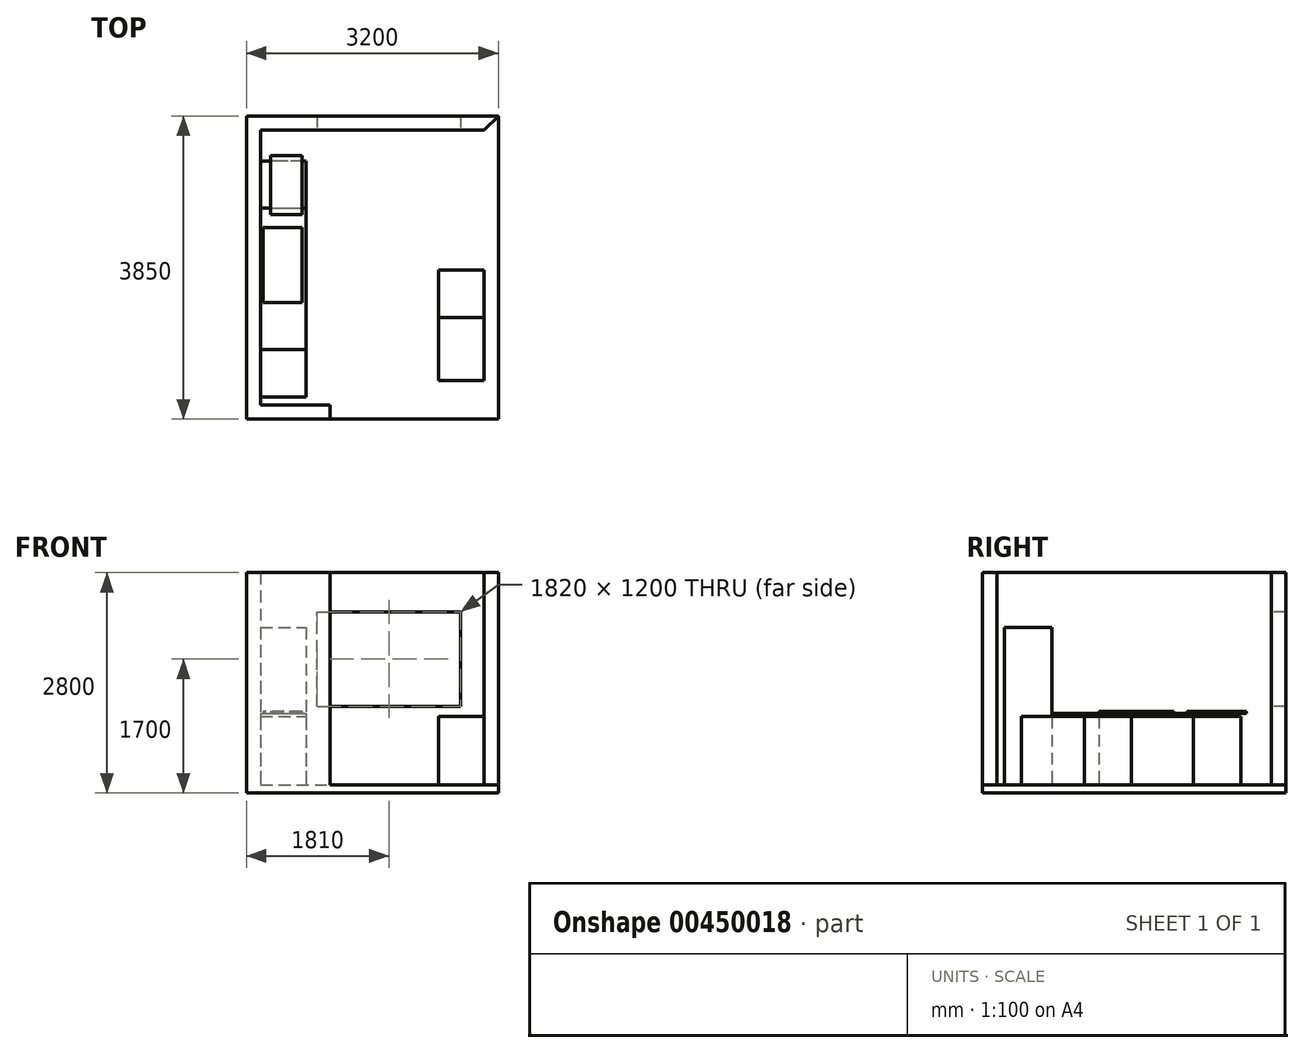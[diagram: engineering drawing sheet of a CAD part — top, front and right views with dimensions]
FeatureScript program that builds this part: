
annotation { "Feature Type Name" : "Feature", "Feature Type Description" : "" }
export const myFeature = defineFeature(function(context is Context, id is Id, definition is map)
    precondition{}
    {
        {
            var Q0;
            Q0=qCreatedBy(makeId("Top.planeOp"),FACE);
            var sketch = newSketch(context, id + "F0", { "sketchPlane" : qUnion([Q0])});
            skLineSegment(sketch, "E0.bottom", {"start": v(0, 0) * mm, "end": v(2840, 0) * mm});
            skLineSegment(sketch, "E0.top", {"start": v(0, 3490) * mm, "end": v(2840, 3490) * mm});
            skLineSegment(sketch, "E0.left", {"start": v(0, 0) * mm, "end": v(0, 3490) * mm});
            skLineSegment(sketch, "E0.right", {"start": v(2840, 0) * mm, "end": v(2840, 3490) * mm});
            skLineSegment(sketch, "E1.0", {"start": v(-180, -180) * mm, "end": v(-180, 3670) * mm});
            skLineSegment(sketch, "E1.1", {"start": v(-180, -180) * mm, "end": v(3020, -180) * mm});
            skLineSegment(sketch, "E1.2", {"start": v(3020, -180) * mm, "end": v(3020, 3670) * mm});
            skLineSegment(sketch, "E1.3", {"start": v(-180, 3670) * mm, "end": v(3020, 3670) * mm});
            skLineSegment(sketch, "E2", {"start": v(2840, 3490) * mm, "end": v(3020, 3670) * mm});
            skLineSegment(sketch, "E3", {"start": v(880, 0) * mm, "end": v(880, -180) * mm});
            skSolve(sketch);
        }
        {
            var Q0;
            Q0=makeQuery(id+"F0.imprint","IMPRINT",FACE,{"disambiguationData":[TD([[makeQuery(id+"F0.imprint","IMPRINT",EDGE,{"derivedFrom":sQuery(id+"F0.wireOp",EDGE,"E0.top")}),1.0]])]});
            var Q1;
            Q1=makeQuery(id+"F0.imprint","IMPRINT",FACE,{"disambiguationData":[TD([[makeQuery(id+"F0.imprint","IMPRINT",EDGE,{"derivedFrom":sQuery(id+"F0.wireOp",EDGE,"E0.top")}),-1.0]])]});
            var Q2;
            {var subQ3=sQuery(id+"F0.wireOp",EDGE,"E0.right");Q2=makeQuery(id+"F0.imprint","IMPRINT",FACE,{"disambiguationData":[TD([[makeQuery(id+"F0.imprint","IMPRINT",EDGE,{"derivedFrom":subQ3}),-1.0]])]});}
            extrude(context, id + "F1", {"entities" : qUnion([Q0, Q1, Q2]), "oppositeDirection" : true, "depth" : 100 * mm});
        }
        {
            var Q0;
            Q0=makeQuery(id+"F0.imprint","IMPRINT",FACE,{"disambiguationData":[TD([[makeQuery(id+"F0.imprint","IMPRINT",EDGE,{"derivedFrom":sQuery(id+"F0.wireOp",EDGE,"E0.top")}),1.0]])]});
            extrude(context, id + "F2", {"entities" : qUnion([Q0]), "operationType" : NewBodyOperationType.ADD, "depth" : 2700 * mm});
        }
        {
            var Q0;
            Q0=makeQuery(id+"F0.imprint","IMPRINT",FACE,{"disambiguationData":[TD([[makeQuery(id+"F0.imprint","IMPRINT",EDGE,{"derivedFrom":sQuery(id+"F0.wireOp",EDGE,"E0.top")}),-1.0]])]});
            var sketch = newSketch(context, id + "F3", { "sketchPlane" : qUnion([Q0])});
            skLineSegment(sketch, "E4.0.0", {"start": v(2840, 3490) * mm, "end": v(0, 3490) * mm});
            skLineSegment(sketch, "E4.0.1", {"start": v(0, 3490) * mm, "end": v(0, 0) * mm});
            skLineSegment(sketch, "E4.0.2", {"start": v(0, 0) * mm, "end": v(880, 0) * mm});
            skLineSegment(sketch, "E4.0.3", {"start": v(880, 0) * mm, "end": v(2840, 0) * mm});
            skLineSegment(sketch, "E4.0.4", {"start": v(2840, 0) * mm, "end": v(2840, 3490) * mm});
            skLineSegment(sketch, "E5.bottom", {"start": v(0, 100) * mm, "end": v(580, 100) * mm});
            skLineSegment(sketch, "E5.top", {"start": v(0, 700) * mm, "end": v(580, 700) * mm});
            skLineSegment(sketch, "E5.left", {"start": v(0, 100) * mm, "end": v(0, 700) * mm});
            skLineSegment(sketch, "E5.right", {"start": v(580, 100) * mm, "end": v(580, 700) * mm});
            skLineSegment(sketch, "E6", {"start": v(580, 700) * mm, "end": v(580, 1300) * mm});
            skLineSegment(sketch, "E7", {"start": v(0, 1300) * mm, "end": v(580, 1300) * mm});
            skLineSegment(sketch, "E8", {"start": v(580, 1300) * mm, "end": v(580, 2500) * mm});
            skLineSegment(sketch, "E9", {"start": v(0, 2500) * mm, "end": v(580, 2500) * mm});
            skLineSegment(sketch, "E10", {"start": v(580, 2500) * mm, "end": v(580, 3100) * mm});
            skLineSegment(sketch, "E11", {"start": v(580, 3100) * mm, "end": v(0, 3100) * mm});
            skLineSegment(sketch, "E12", {"start": v(0, 700) * mm, "end": v(0, 100) * mm});
            skLineSegment(sketch, "E13", {"start": v(0, 700) * mm, "end": v(0, 1300) * mm});
            skLineSegment(sketch, "E14", {"start": v(580, 1300) * mm, "end": v(580, 700) * mm});
            skLineSegment(sketch, "E15", {"start": v(0, 1300) * mm, "end": v(0, 2500) * mm});
            skLineSegment(sketch, "E16", {"start": v(580, 2500) * mm, "end": v(580, 1300) * mm});
            skLineSegment(sketch, "E17", {"start": v(0, 2500) * mm, "end": v(0, 3100) * mm});
            skLineSegment(sketch, "E18", {"start": v(0, 3100) * mm, "end": v(580, 3100) * mm});
            skLineSegment(sketch, "E19", {"start": v(580, 3100) * mm, "end": v(580, 2500) * mm});
            skSolve(sketch);
        }
        {
            var Q0;
            Q0=makeQuery(id+"F3.imprint","IMPRINT",FACE,{"disambiguationData":[TD([[makeQuery(id+"F3.imprint","IMPRINT",EDGE,{"derivedFrom":sQuery(id+"F3.wireOp",EDGE,"E5.bottom")}),1.0]])]});
            extrude(context, id + "F4", {"entities" : qUnion([Q0]), "depth" : 2000 * mm});
        }
        {
            var Q0;
            Q0=makeQuery(id+"F3.imprint","IMPRINT",FACE,{"disambiguationData":[TD([[makeQuery(id+"F3.imprint","IMPRINT",EDGE,{"derivedFrom":sQuery(id+"F3.wireOp",EDGE,"E5.top")}),1.0]])]});
            extrude(context, id + "F5", {"entities" : qUnion([Q0]), "depth" : 870 * mm});
        }
        {
            var Q0;
            Q0=makeQuery(id+"F3.imprint","IMPRINT",FACE,{"disambiguationData":[TD([[makeQuery(id+"F3.imprint","IMPRINT",EDGE,{"derivedFrom":sQuery(id+"F3.wireOp",EDGE,"E7")}),1.0]])]});
            extrude(context, id + "F6", {"entities" : qUnion([Q0]), "depth" : 870 * mm});
        }
        {
            var Q0;
            Q0=makeQuery(id+"F3.imprint","IMPRINT",FACE,{"disambiguationData":[TD([[makeQuery(id+"F3.imprint","IMPRINT",EDGE,{"derivedFrom":sQuery(id+"F3.wireOp",EDGE,"E9")}),1.0]])]});
            extrude(context, id + "F7", {"entities" : qUnion([Q0]), "depth" : 870 * mm});
        }
        {
            var Q0;
            Q0=makeQuery(id+"F6.opExtrude","CAP_FACE",FACE,{"disambiguationData":[OSD([sQuery(id+"F3.wireOp",EDGE,"E7"),sQuery(id+"F3.wireOp",EDGE,"E15"),sQuery(id+"F3.wireOp",EDGE,"E9"),sQuery(id+"F3.wireOp",EDGE,"E16")])],"isStart":false});
            var sketch = newSketch(context, id + "F8", { "sketchPlane" : qUnion([Q0])});
            skLineSegment(sketch, "E20.0", {"start": v(0, 700) * mm, "end": v(580, 700) * mm});
            skLineSegment(sketch, "E21.0", {"start": v(0, 700) * mm, "end": v(0, 1300) * mm});
            skPoint(sketch, "E22.0", {"position": v(0, 3490) * mm});
            skLineSegment(sketch, "E23.0", {"start": v(580, 1300) * mm, "end": v(580, 700) * mm});
            skLineSegment(sketch, "E24.0", {"start": v(2840, 3490) * mm, "end": v(0, 3490) * mm});
            skLineSegment(sketch, "E25", {"start": v(580, 700) * mm, "end": v(580, 3490) * mm});
            skLineSegment(sketch, "E26", {"start": v(580, 3490) * mm, "end": v(0, 3490) * mm});
            skLineSegment(sketch, "E27", {"start": v(0, 2500) * mm, "end": v(0, 3490) * mm});
            skSolve(sketch);
        }
        {
            var Q0;
            {var subQ2=sQuery(id+"F8.wireOp",EDGE,"E26");Q0=makeQuery(id+"F8.imprint","IMPRINT",FACE,{"disambiguationData":[TD([[makeQuery(id+"F8.imprint","IMPRINT",EDGE,{"derivedFrom":subQ2}),1.0]])]});}
            var Q1;
            {var subQ1=makeQuery(id+"F6.opExtrude","CAP_EDGE",EDGE,{"disambiguationData":[OSD([sQuery(id+"F3.wireOp",EDGE,"E7")])],"isStart":false});Q1=makeQuery(id+"F8.imprint","IMPRINT",FACE,{"disambiguationData":[TD([[makeQuery(id+"F8.imprint","IMPRINT",EDGE,{"derivedFrom":subQ1}),1.0]])]});}
            var Q2;
            Q2=makeQuery(id+"F8.imprint","IMPRINT",FACE,{"disambiguationData":[TD([[makeQuery(id+"F8.imprint","IMPRINT",EDGE,{"derivedFrom":sQuery(id+"F8.wireOp",EDGE,"E21.0")}),-1.0]])]});
            extrude(context, id + "F9", {"entities" : qUnion([Q0, Q1, Q2]), "depth" : 40 * mm});
        }
        {
            var Q0;
            Q0=makeQuery(id+"F9.opExtrude","CAP_FACE",FACE,{"disambiguationData":[OSD([sQuery(id+"F3.wireOp",EDGE,"E15"),sQuery(id+"F8.wireOp",EDGE,"E21.0"),sQuery(id+"F8.wireOp",EDGE,"E20.0"),sQuery(id+"F8.wireOp",EDGE,"E25"),sQuery(id+"F8.wireOp",EDGE,"E26"),sQuery(id+"F8.wireOp",EDGE,"E27")])],"isStart":false});
            var sketch = newSketch(context, id + "F10", { "sketchPlane" : qUnion([Q0])});
            skLineSegment(sketch, "E28.0", {"start": v(580, 3100) * mm, "end": v(0, 3100) * mm});
            skLineSegment(sketch, "E29.0", {"start": v(0, 2500) * mm, "end": v(580, 2500) * mm});
            skPoint(sketch, "E30.0", {"position": v(580, 2800) * mm});
            skLineSegment(sketch, "E31.bottom", {"start": v(130, 3167.5) * mm, "end": v(530, 3167.5) * mm});
            skLineSegment(sketch, "E31.top", {"start": v(130, 2417.5) * mm, "end": v(530, 2417.5) * mm});
            skLineSegment(sketch, "E31.left", {"start": v(130, 3167.5) * mm, "end": v(130, 2417.5) * mm});
            skLineSegment(sketch, "E31.right", {"start": v(530, 3167.5) * mm, "end": v(530, 2417.5) * mm});
            skSolve(sketch);
        }
        {
            var Q0;
            {var subQ5=sQuery(id+"F10.wireOp",EDGE,"E31.bottom");Q0=makeQuery(id+"F10.imprint","IMPRINT",FACE,{"disambiguationData":[TD([[makeQuery(id+"F10.imprint","IMPRINT",EDGE,{"derivedFrom":subQ5}),-1.0]])]});}
            var Q1;
            {var subQ0=sQuery(id+"F10.wireOp",EDGE,"E31.right");var subQ1=sQuery(id+"F10.wireOp",EDGE,"E28.0");var subQ2=makeQuery(id+"F10.imprint","INTERSECT",VERTEX,{"derivedFrom":[subQ1,subQ0]});Q1=makeQuery(id+"F10.imprint","IMPRINT",FACE,{"disambiguationData":[TD([[makeQuery(id+"F10.imprint","IMPRINT",EDGE,{"disambiguationData":[TD([[subQ2,-1.0]])],"derivedFrom":subQ1}),1.0]])]});}
            var Q2;
            {var subQ5=sQuery(id+"F10.wireOp",EDGE,"E31.top");Q2=makeQuery(id+"F10.imprint","IMPRINT",FACE,{"disambiguationData":[TD([[makeQuery(id+"F10.imprint","IMPRINT",EDGE,{"derivedFrom":subQ5}),1.0]])]});}
            extrude(context, id + "F11", {"entities" : qUnion([Q0, Q1, Q2]), "depth" : 25 * mm});
        }
        {
            var Q0;
            Q0=makeQuery(id+"F9.opExtrude","CAP_FACE",FACE,{"disambiguationData":[OSD([sQuery(id+"F3.wireOp",EDGE,"E15"),sQuery(id+"F8.wireOp",EDGE,"E21.0"),sQuery(id+"F8.wireOp",EDGE,"E20.0"),sQuery(id+"F8.wireOp",EDGE,"E25"),sQuery(id+"F8.wireOp",EDGE,"E26"),sQuery(id+"F8.wireOp",EDGE,"E27")])],"isStart":false});
            var sketch = newSketch(context, id + "F12", { "sketchPlane" : qUnion([Q0])});
            skLineSegment(sketch, "E32.0", {"start": v(0, 1300) * mm, "end": v(580, 1300) * mm, "construction": true});
            skLineSegment(sketch, "E33.0", {"start": v(580, 1300) * mm, "end": v(580, 2500) * mm, "construction": true});
            skLineSegment(sketch, "E34.0", {"start": v(0, 2500) * mm, "end": v(580, 2500) * mm, "construction": true});
            skLineSegment(sketch, "E35.bottom", {"start": v(530, 1300) * mm, "end": v(30, 1300) * mm, "construction": true});
            skLineSegment(sketch, "E35.top", {"start": v(530, 2250) * mm, "end": v(30, 2250) * mm, "construction": true});
            skLineSegment(sketch, "E35.left", {"start": v(530, 1300) * mm, "end": v(530, 2250) * mm, "construction": true});
            skLineSegment(sketch, "E35.right", {"start": v(30, 1300) * mm, "end": v(30, 2250) * mm, "construction": true});
            skLineSegment(sketch, "E36.bottom", {"start": v(30, 1598.45) * mm, "end": v(0, 1598.45) * mm, "construction": true});
            skLineSegment(sketch, "E36.top", {"start": v(30, 1567.57) * mm, "end": v(0, 1567.57) * mm, "construction": true});
            skLineSegment(sketch, "E36.left", {"start": v(30, 1598.45) * mm, "end": v(30, 1567.57) * mm, "construction": true});
            skLineSegment(sketch, "E36.right", {"start": v(0, 1598.45) * mm, "end": v(0, 1567.57) * mm, "construction": true});
            skLineSegment(sketch, "E37.bottom", {"start": v(530, 1300) * mm, "end": v(30, 1300) * mm});
            skLineSegment(sketch, "E37.top", {"start": v(530, 2250) * mm, "end": v(30, 2250) * mm});
            skLineSegment(sketch, "E37.left", {"start": v(530, 1300) * mm, "end": v(530, 2250) * mm});
            skLineSegment(sketch, "E37.right", {"start": v(30, 1300) * mm, "end": v(30, 2250) * mm});
            skSolve(sketch);
        }
        {
            var Q0;
            Q0=makeQuery(id+"F12.imprint","IMPRINT",FACE,{"disambiguationData":[TD([[makeQuery(id+"F12.imprint","IMPRINT",EDGE,{"derivedFrom":sQuery(id+"F12.wireOp",EDGE,"E37.bottom")}),-1.0]])]});
            extrude(context, id + "F13", {"entities" : qUnion([Q0]), "depth" : 25 * mm});
        }
        {
            var Q0;
            Q0=makeQuery(id+"F0.imprint","IMPRINT",FACE,{"disambiguationData":[TD([[makeQuery(id+"F0.imprint","IMPRINT",EDGE,{"derivedFrom":sQuery(id+"F0.wireOp",EDGE,"E0.top")}),-1.0]])]});
            var sketch = newSketch(context, id + "F14", { "sketchPlane" : qUnion([Q0])});
            skLineSegment(sketch, "E38.0", {"start": v(880, 0) * mm, "end": v(2840, 0) * mm, "construction": true});
            skLineSegment(sketch, "E39.0", {"start": v(2840, 0) * mm, "end": v(2840, 3490) * mm, "construction": true});
            skLineSegment(sketch, "E40.bottom", {"start": v(2840, 0) * mm, "end": v(2040, 0) * mm});
            skLineSegment(sketch, "E40.top", {"start": v(2840, 210) * mm, "end": v(2040, 210) * mm});
            skLineSegment(sketch, "E40.left", {"start": v(2840, 0) * mm, "end": v(2840, 210) * mm});
            skLineSegment(sketch, "E40.right", {"start": v(2040, 0) * mm, "end": v(2040, 210) * mm});
            skLineSegment(sketch, "E41.bottom", {"start": v(2840, 310) * mm, "end": v(2260, 310) * mm});
            skLineSegment(sketch, "E41.top", {"start": v(2840, 1110) * mm, "end": v(2260, 1110) * mm});
            skLineSegment(sketch, "E41.left", {"start": v(2840, 310) * mm, "end": v(2840, 1110) * mm});
            skLineSegment(sketch, "E41.right", {"start": v(2260, 310) * mm, "end": v(2260, 1110) * mm});
            skLineSegment(sketch, "E42.top", {"start": v(2840, 1710) * mm, "end": v(2260, 1710) * mm});
            skLineSegment(sketch, "E42.left", {"start": v(2840, 1110) * mm, "end": v(2840, 1710) * mm});
            skLineSegment(sketch, "E42.right", {"start": v(2260, 1110) * mm, "end": v(2260, 1710) * mm});
            skSolve(sketch);
        }
        {
            var Q0;
            Q0=makeQuery(id+"F14.imprint","IMPRINT",FACE,{"disambiguationData":[TD([[makeQuery(id+"F14.imprint","IMPRINT",EDGE,{"derivedFrom":sQuery(id+"F14.wireOp",EDGE,"E41.bottom")}),-1.0]])]});
            extrude(context, id + "F15", {"entities" : qUnion([Q0]), "depth" : 870 * mm});
        }
        {
            var Q0;
            Q0=makeQuery(id+"F14.imprint","IMPRINT",FACE,{"disambiguationData":[TD([[makeQuery(id+"F14.imprint","IMPRINT",EDGE,{"derivedFrom":sQuery(id+"F14.wireOp",EDGE,"E41.top")}),-1.0]])]});
            extrude(context, id + "F16", {"entities" : qUnion([Q0]), "depth" : 870 * mm});
        }
        {
            var Q0;
            Q0=makeQuery(id+"F2.opExtrude","SWEPT_FACE",FACE,{"disambiguationData":[OSD([sQuery(id+"F0.wireOp",EDGE,"E0.top")])]});
            var sketch = newSketch(context, id + "F17", { "sketchPlane" : qUnion([Q0])});
            skLineSegment(sketch, "E43.bottom", {"start": v(720, 1000) * mm, "end": v(2540, 1000) * mm});
            skLineSegment(sketch, "E43.top", {"start": v(720, 2200) * mm, "end": v(2540, 2200) * mm});
            skLineSegment(sketch, "E43.left", {"start": v(720, 1000) * mm, "end": v(720, 2200) * mm});
            skLineSegment(sketch, "E43.right", {"start": v(2540, 1000) * mm, "end": v(2540, 2200) * mm});
            skSolve(sketch);
        }
        {
            var Q0;
            Q0=makeQuery(id+"F17.imprint","IMPRINT",FACE,{"disambiguationData":[TD([[makeQuery(id+"F17.imprint","IMPRINT",EDGE,{"derivedFrom":sQuery(id+"F17.wireOp",EDGE,"E43.bottom")}),1.0]])]});
            extrude(context, id + "F18", {"entities" : qUnion([Q0]), "operationType" : NewBodyOperationType.REMOVE, "endBound" : BoundingType.THROUGH_ALL, "oppositeDirection" : true, "depth" : 25 * mm});
        }
    });
